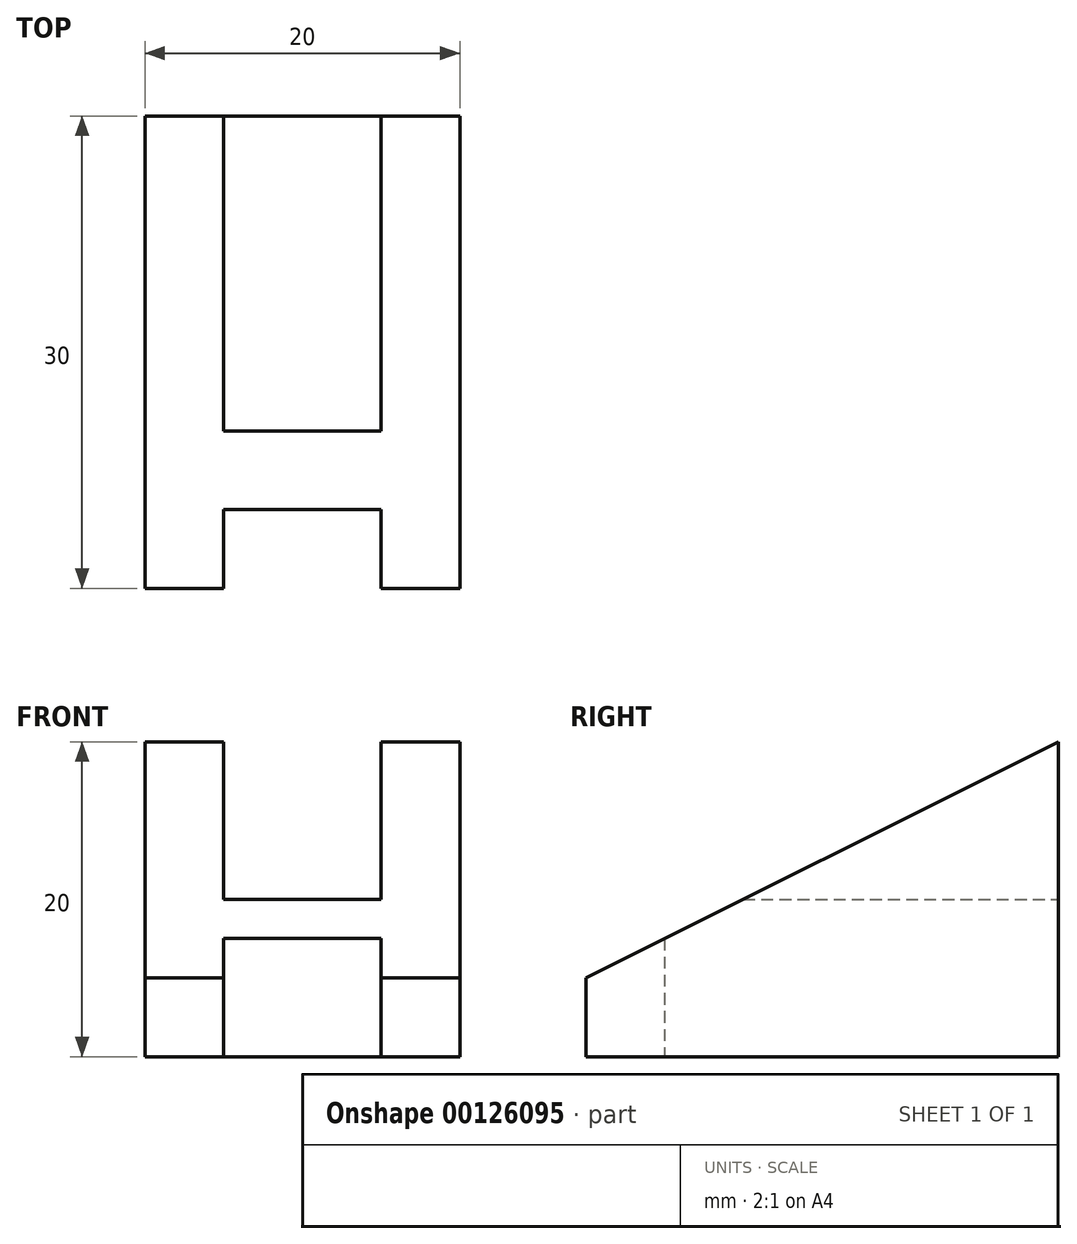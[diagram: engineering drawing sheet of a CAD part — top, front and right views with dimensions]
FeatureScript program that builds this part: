
annotation { "Feature Type Name" : "Feature", "Feature Type Description" : "" }
export const myFeature = defineFeature(function(context is Context, id is Id, definition is map)
    precondition{}
    {
        {
            var Q0;
            Q0=qCreatedBy(makeId("Top.planeOp"),FACE);
            var sketch = newSketch(context, id + "F0", { "sketchPlane" : qUnion([Q0])});
            skLineSegment(sketch, "E0", {"start": v(0, 0) * mm, "end": v(0, 30) * mm});
            skLineSegment(sketch, "E1", {"start": v(0, 30) * mm, "end": v(5, 30) * mm});
            skLineSegment(sketch, "E2", {"start": v(5, 30) * mm, "end": v(5, 10) * mm});
            skLineSegment(sketch, "E3", {"start": v(5, 10) * mm, "end": v(15, 10) * mm});
            skLineSegment(sketch, "E4", {"start": v(15, 10) * mm, "end": v(15, 30) * mm});
            skLineSegment(sketch, "E5", {"start": v(15, 30) * mm, "end": v(20, 30) * mm});
            skLineSegment(sketch, "E6", {"start": v(20, 30) * mm, "end": v(20, 0) * mm});
            skLineSegment(sketch, "E7", {"start": v(20, 0) * mm, "end": v(15, 0) * mm});
            skLineSegment(sketch, "E8", {"start": v(15, 0) * mm, "end": v(15, 5) * mm});
            skLineSegment(sketch, "E9", {"start": v(15, 5) * mm, "end": v(5, 5) * mm});
            skLineSegment(sketch, "E10", {"start": v(5, 5) * mm, "end": v(5, 0) * mm});
            skLineSegment(sketch, "E11", {"start": v(5, 0) * mm, "end": v(0, 0) * mm});
            skLineSegment(sketch, "E12", {"start": v(5, 30) * mm, "end": v(15, 30) * mm});
            skSolve(sketch);
        }
        {
            var Q0;
            Q0=makeQuery(id+"F0.imprint","IMPRINT",FACE,{"disambiguationData":[TD([[makeQuery(id+"F0.imprint","IMPRINT",EDGE,{"derivedFrom":sQuery(id+"F0.wireOp",EDGE,"E0")}),-1.0]])]});
            extrude(context, id + "F1", {"entities" : qUnion([Q0]), "depth" : 20 * mm});
        }
        {
            var Q0;
            Q0=makeQuery(id+"F0.imprint","IMPRINT",FACE,{"disambiguationData":[TD([[makeQuery(id+"F0.imprint","IMPRINT",EDGE,{"derivedFrom":sQuery(id+"F0.wireOp",EDGE,"E2")}),1.0]])]});
            extrude(context, id + "F2", {"entities" : qUnion([Q0]), "operationType" : NewBodyOperationType.ADD, "depth" : 10 * mm});
        }
        {
            var Q0;
            Q0=qCreatedBy(makeId("Right.planeOp"),FACE);
            var sketch = newSketch(context, id + "F3", { "sketchPlane" : qUnion([Q0])});
            skLineSegment(sketch, "E13", {"start": v(0, 0) * mm, "end": v(0, 5) * mm});
            skLineSegment(sketch, "E14", {"start": v(0, 5) * mm, "end": v(30, 20) * mm});
            skLineSegment(sketch, "E15", {"start": v(30, 20) * mm, "end": v(30, 0) * mm});
            skLineSegment(sketch, "E16", {"start": v(30, 0) * mm, "end": v(0, 0) * mm});
            skLineSegment(sketch, "E17", {"start": v(0, 5) * mm, "end": v(0, 20) * mm});
            skLineSegment(sketch, "E18", {"start": v(0, 20) * mm, "end": v(30, 20) * mm});
            skSolve(sketch);
        }
        {
            var Q0;
            Q0=makeQuery(id+"F3.imprint","IMPRINT",FACE,{"disambiguationData":[TD([[makeQuery(id+"F3.imprint","IMPRINT",EDGE,{"derivedFrom":sQuery(id+"F3.wireOp",EDGE,"E14")}),1.0]])]});
            extrude(context, id + "F4", {"entities" : qUnion([Q0]), "operationType" : NewBodyOperationType.REMOVE, "endBound" : BoundingType.THROUGH_ALL, "depth" : 25 * mm});
        }
    });
